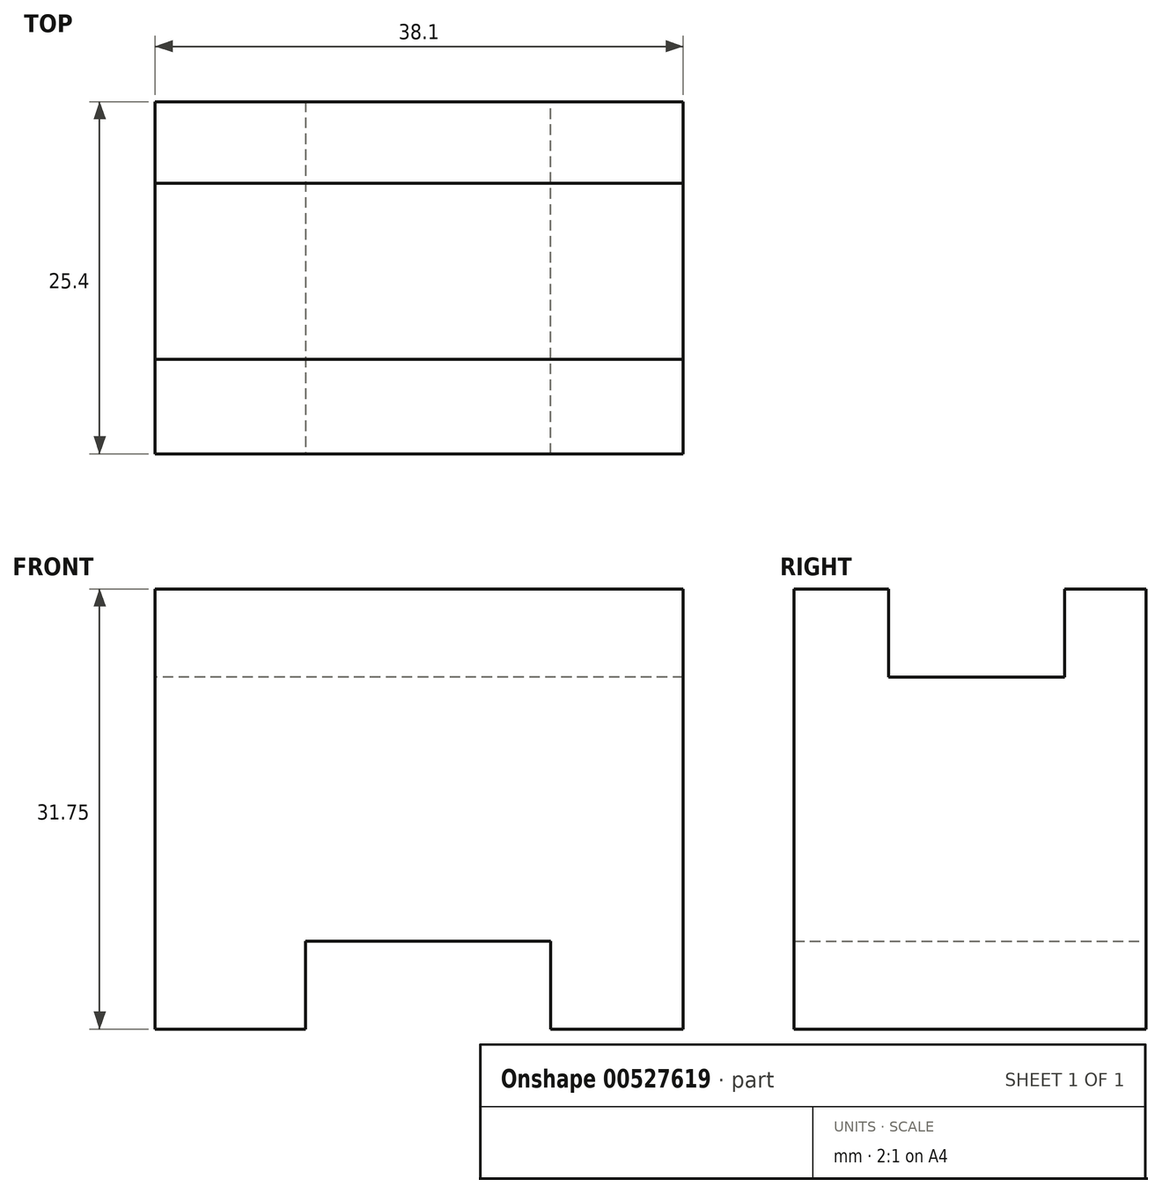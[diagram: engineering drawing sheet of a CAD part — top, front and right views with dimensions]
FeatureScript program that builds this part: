
annotation { "Feature Type Name" : "Feature", "Feature Type Description" : "" }
export const myFeature = defineFeature(function(context is Context, id is Id, definition is map)
    precondition{}
    {
        {
            var Q0;
            Q0=qCreatedBy(makeId("Right.planeOp"),FACE);
            var sketch = newSketch(context, id + "F0", { "sketchPlane" : qUnion([Q0])});
            skLineSegment(sketch, "E0", {"start": v(0, 0) * mm, "end": v(25.4, 0) * mm});
            skLineSegment(sketch, "E1", {"start": v(25.4, 0) * mm, "end": v(25.4, 31.75) * mm});
            skLineSegment(sketch, "E2", {"start": v(25.4, 31.75) * mm, "end": v(0, 31.75) * mm});
            skLineSegment(sketch, "E3", {"start": v(0, 31.75) * mm, "end": v(0, 0) * mm});
            skSolve(sketch);
        }
        {
            var Q0;
            Q0=makeQuery(id+"F0.imprint","IMPRINT",FACE,{"disambiguationData":[TD([[makeQuery(id+"F0.imprint","IMPRINT",EDGE,{"derivedFrom":sQuery(id+"F0.wireOp",EDGE,"E0")}),1.0]])]});
            extrude(context, id + "F1", {"entities" : qUnion([Q0]), "depth" : 38.1 * mm, "offsetDistance" : 25.4 * mm});
        }
        {
            var Q0;
            Q0=makeQuery(id+"F1.opExtrude","SWEPT_FACE",FACE,{"disambiguationData":[OSD([sQuery(id+"F0.wireOp",EDGE,"E2")])]});
            var sketch = newSketch(context, id + "F2", { "sketchPlane" : qUnion([Q0])});
            skLineSegment(sketch, "E4", {"start": v(38.1, 19.52) * mm, "end": v(0, 19.52) * mm});
            skLineSegment(sketch, "E5", {"start": v(0, 19.52) * mm, "end": v(0, 6.82) * mm});
            skLineSegment(sketch, "E6", {"start": v(0, 6.82) * mm, "end": v(38.1, 6.82) * mm});
            skLineSegment(sketch, "E7", {"start": v(38.1, 6.82) * mm, "end": v(38.1, 19.52) * mm});
            skSolve(sketch);
        }
        {
            var Q0;
            Q0=makeQuery(id+"F2.imprint","IMPRINT",FACE,{"disambiguationData":[TD([[makeQuery(id+"F2.imprint","IMPRINT",EDGE,{"derivedFrom":sQuery(id+"F2.wireOp",EDGE,"E4")}),1.0]])]});
            extrude(context, id + "F3", {"entities" : qUnion([Q0]), "operationType" : NewBodyOperationType.REMOVE, "oppositeDirection" : true, "depth" : 6.35 * mm, "offsetDistance" : 25.4 * mm});
        }
        {
            var Q0;
            Q0=makeQuery(id+"F1.opExtrude","SWEPT_FACE",FACE,{"disambiguationData":[OSD([sQuery(id+"F0.wireOp",EDGE,"E0")])]});
            var sketch = newSketch(context, id + "F4", { "sketchPlane" : qUnion([Q0])});
            skLineSegment(sketch, "E8", {"start": v(28.53, 0) * mm, "end": v(28.53, -25.4) * mm});
            skLineSegment(sketch, "E9", {"start": v(28.53, -25.4) * mm, "end": v(10.85, -25.4) * mm});
            skLineSegment(sketch, "E10", {"start": v(10.85, -25.4) * mm, "end": v(10.85, 0) * mm});
            skLineSegment(sketch, "E11", {"start": v(10.85, 0) * mm, "end": v(28.53, 0) * mm});
            skSolve(sketch);
        }
        {
            var Q0;
            Q0=makeQuery(id+"F4.imprint","IMPRINT",FACE,{"disambiguationData":[TD([[makeQuery(id+"F4.imprint","IMPRINT",EDGE,{"derivedFrom":sQuery(id+"F4.wireOp",EDGE,"E8")}),-1.0]])]});
            extrude(context, id + "F5", {"entities" : qUnion([Q0]), "operationType" : NewBodyOperationType.REMOVE, "oppositeDirection" : true, "depth" : 6.35 * mm, "offsetDistance" : 25.4 * mm});
        }
    });
